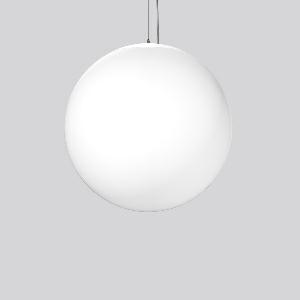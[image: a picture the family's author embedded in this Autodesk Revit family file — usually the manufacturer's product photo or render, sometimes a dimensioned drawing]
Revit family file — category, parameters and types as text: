
# Revit family: basic_ball_312107_002_76_ead0
name_source: partatom
category: Lighting Fixtures
units: mm (PartAtom-declared; Revit-internal decimal feet)

## family parameters
Cut with Voids When Loaded = No
Host = Face
Light Source = No
Part Type = Normal
Room Calculation Point = No
Round Connector Dimension = Use Diameter
Shared = No

## types (1)
- BASIC BALL (1 x LED Modul 930, 8400 lm, 3000)
    Apparent Load = 79 VA
    CIE Flux Codes = 25 51 76 56 100
    Color Rendering = 90
    Color Temperature = 3000
    Default Elevation = 1800 mm
    Description = Series: BASIC BALL
Pendant luminaire in timelessly classic sphere design. Canopy: metal, powder-coated, white. Metal cap: white, powder-coated. Diffuser: mouth-blown opal glass, satin finish. Shadow-free, homogeneous and soft illumination. Single-point steel cable suspension, steplessly adjustable. Special lengths available on request. Power supply cable: white. 
Colour: white
Diameter: 500 mm
Height: 500 mm
Suspension length: 300-4000 mm
Lamp: LED
Socket: without socket
Colour temperature: 3000K
Colour rendering index (CRI): 90
System power: 79 W
Rated luminous flux: 8400 lm
Luminous efficiency: 106 lm/W
Control gear: Converter, dimmable, DALI
Protection class: I
Type of protection: IP 40
    Height = 500 mm
    Lamp = 1 x LED Modul 930
    Lamp Light Flux = 8400 lm
    Lamp count = 1
    Length = 500 mm
    Lifetime = 50000 h
    Luminous efficacy = 106 lm/W
    Manufacturer = RZB
    ModVariant = No
    Model = 312107.002.76
    Mounting Place = Ceiling
    Mounting Type = Pendant
    Number of Poles = 1
    OnlyDefault = Yes
    Power Factor = 1
    Product Name = BASIC BALL
    Product group = Pendant luminaires
    ProductGroupID = 902
    Protection Class = Protection class I
    Protection Degree = IP 40
    RLX_Detail_Level = 1
    RLX_Emergency_Light_Flux = 0 lm
    RLX_Emergency_Type = 0
    RLX_Emergency_Type_DB = No
    RlxData = <blob elided: 51801 chars, md5=cdf553eb>
    Socket = socket
    Standby Power = 0 W
    System Light Flux = 8400 lm
    System Power = 79 W
    Type Comments = Product without accessories
    Type Image = 312107.002.jpg
    URL = http://relux.com
    VarID = ---
    Voltage = 230 V
    Voltage Range = 220-240 V
    Weight = 0.00 kg
    Width = 0 mm  [stored 0 ft]

note: [stored X ft] marks values corroborated as IEEE doubles in the binary element streams (Revit-internal decimal feet)

## geometry (parser evidence)
native form markers: Blend x4, Sweep x14
no freeform markers — native parametric forms only
